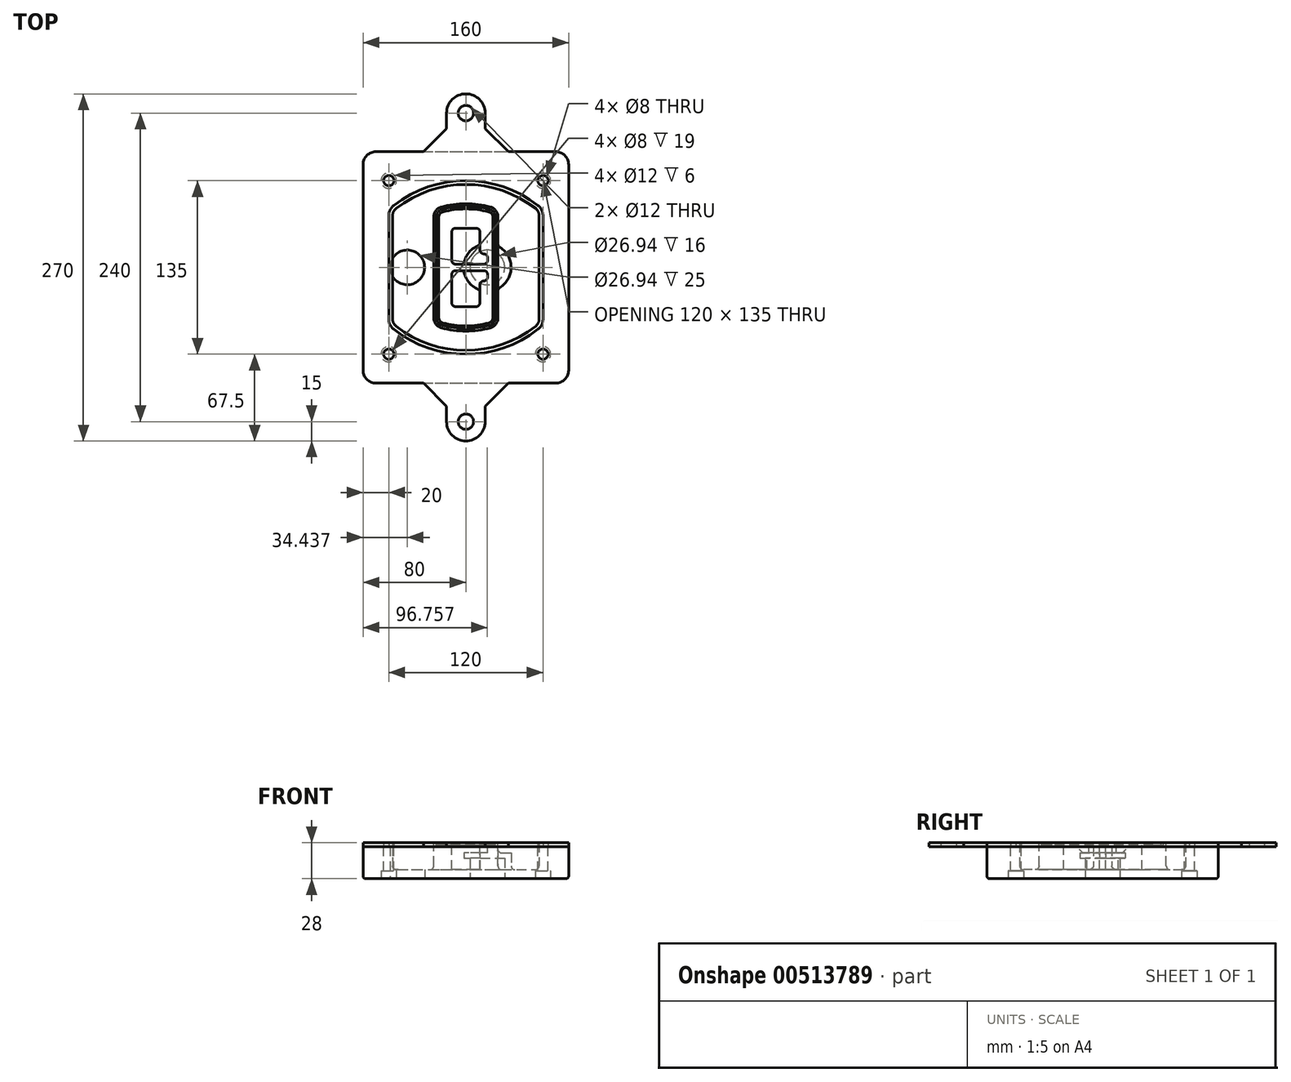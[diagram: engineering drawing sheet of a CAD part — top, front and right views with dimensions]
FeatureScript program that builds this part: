
annotation { "Feature Type Name" : "Feature", "Feature Type Description" : "" }
export const myFeature = defineFeature(function(context is Context, id is Id, definition is map)
    precondition{}
    {
        {
            var Q0;
            Q0=qCreatedBy(makeId("Top.planeOp"),FACE);
            var sketch = newSketch(context, id + "F0", { "sketchPlane" : qUnion([Q0])});
            skPoint(sketch, "E0.rect.middle", {"position": v(0, 0) * mm});
            skLineSegment(sketch, "E1.bottom", {"start": v(-70, -90) * mm, "end": v(70, -90) * mm});
            skLineSegment(sketch, "E1.top", {"start": v(-70, 90) * mm, "end": v(70, 90) * mm});
            skLineSegment(sketch, "E1.left", {"start": v(-80, -80) * mm, "end": v(-80, 80) * mm});
            skLineSegment(sketch, "E1.right", {"start": v(80, -80) * mm, "end": v(80, 80) * mm});
            skLineSegment(sketch, "E2", {"start": v(-80, 90) * mm, "end": v(80, -90) * mm, "construction": true});
            skLineSegment(sketch, "E3", {"start": v(80, 90) * mm, "end": v(-80, -90) * mm, "construction": true});
            skCircle(sketch, "E4", {"center": v(-60, 67.5) * mm, "radius": 4 * mm});
            skCircle(sketch, "E5", {"center": v(60, 67.5) * mm, "radius": 4 * mm});
            skCircle(sketch, "E6", {"center": v(60, -67.5) * mm, "radius": 4 * mm});
            skCircle(sketch, "E7", {"center": v(-60, -67.5) * mm, "radius": 4 * mm});
            skLineSegment(sketch, "E8", {"start": v(-60, 67.5) * mm, "end": v(60, 67.5) * mm, "construction": true});
            skLineSegment(sketch, "E9", {"start": v(60, 67.5) * mm, "end": v(60, -67.5) * mm, "construction": true});
            skLineSegment(sketch, "E10", {"start": v(60, -67.5) * mm, "end": v(-60, -67.5) * mm, "construction": true});
            skLineSegment(sketch, "E11", {"start": v(-60, -67.5) * mm, "end": v(-60, 67.5) * mm, "construction": true});
            skLineSegment(sketch, "E12", {"start": v(-60, 40.3) * mm, "end": v(-60, -40.3) * mm});
            skLineSegment(sketch, "E13", {"start": v(60, 40.3) * mm, "end": v(60, -40.3) * mm});
            skArc(sketch, "E14", {"start": v(56.15, 48.18) * mm, "mid": v(0, 67.5) * mm, "end": v(-56.15, 48.18) * mm});
            skArc(sketch, "E15", {"start": v(-56.15, -48.18) * mm, "mid": v(0, -67.5) * mm, "end": v(56.15, -48.18) * mm});
            skLineSegment(sketch, "E16", {"start": v(-60, 0) * mm, "end": v(60, 0) * mm, "construction": true});
            skPoint(sketch, "E17.visualSharp", {"position": v(-60, -45) * mm});
            skArc(sketch, "E17.filletArc", {"start": v(-60, -40.3) * mm, "mid": v(-58.99, -44.68) * mm, "end": v(-56.15, -48.18) * mm});
            skPoint(sketch, "E18.visualSharp", {"position": v(-60, 45) * mm});
            skArc(sketch, "E18.filletArc", {"start": v(-56.15, 48.18) * mm, "mid": v(-58.99, 44.68) * mm, "end": v(-60, 40.3) * mm});
            skPoint(sketch, "E19.visualSharp", {"position": v(60, 45) * mm});
            skArc(sketch, "E19.filletArc", {"start": v(60, 40.3) * mm, "mid": v(58.99, 44.68) * mm, "end": v(56.15, 48.18) * mm});
            skPoint(sketch, "E20.visualSharp", {"position": v(60, -45) * mm});
            skArc(sketch, "E20.filletArc", {"start": v(56.15, -48.18) * mm, "mid": v(58.99, -44.68) * mm, "end": v(60, -40.3) * mm});
            skPoint(sketch, "E21.visualSharp", {"position": v(-80, 90) * mm});
            skArc(sketch, "E21.filletArc", {"start": v(-70, 90) * mm, "mid": v(-77.07, 87.07) * mm, "end": v(-80, 80) * mm});
            skPoint(sketch, "E22.visualSharp", {"position": v(80, 90) * mm});
            skArc(sketch, "E22.filletArc", {"start": v(80, 80) * mm, "mid": v(77.07, 87.07) * mm, "end": v(70, 90) * mm});
            skPoint(sketch, "E23.visualSharp", {"position": v(80, -90) * mm});
            skArc(sketch, "E23.filletArc", {"start": v(70, -90) * mm, "mid": v(77.07, -87.07) * mm, "end": v(80, -80) * mm});
            skPoint(sketch, "E24.visualSharp", {"position": v(-80, -90) * mm});
            skArc(sketch, "E24.filletArc", {"start": v(-80, -80) * mm, "mid": v(-77.07, -87.07) * mm, "end": v(-70, -90) * mm});
            skArc(sketch, "E25.0", {"start": v(57, 40.3) * mm, "mid": v(56.3, 43.36) * mm, "end": v(54.3, 45.81) * mm});
            skLineSegment(sketch, "E25.1", {"start": v(57, 40.3) * mm, "end": v(57, -40.3) * mm});
            skArc(sketch, "E25.2", {"start": v(54.3, -45.81) * mm, "mid": v(56.3, -43.36) * mm, "end": v(57, -40.3) * mm});
            skArc(sketch, "E25.3", {"start": v(-54.3, -45.81) * mm, "mid": v(0, -64.5) * mm, "end": v(54.3, -45.81) * mm});
            skArc(sketch, "E25.4", {"start": v(-57, -40.3) * mm, "mid": v(-56.3, -43.36) * mm, "end": v(-54.3, -45.81) * mm});
            skArc(sketch, "E25.5", {"start": v(54.3, 45.81) * mm, "mid": v(0, 64.5) * mm, "end": v(-54.3, 45.81) * mm});
            skLineSegment(sketch, "E25.6", {"start": v(-57, 40.3) * mm, "end": v(-57, -40.3) * mm});
            skArc(sketch, "E25.7", {"start": v(-54.3, 45.81) * mm, "mid": v(-56.3, 43.36) * mm, "end": v(-57, 40.3) * mm});
            skArc(sketch, "E26.0", {"start": v(-58.62, 51.33) * mm, "mid": v(-62.58, 46.43) * mm, "end": v(-64, 40.3) * mm});
            skArc(sketch, "E26.1", {"start": v(58.62, 51.33) * mm, "mid": v(0, 71.5) * mm, "end": v(-58.62, 51.33) * mm});
            skArc(sketch, "E26.2", {"start": v(64, 40.3) * mm, "mid": v(62.58, 46.43) * mm, "end": v(58.62, 51.33) * mm});
            skLineSegment(sketch, "E26.3", {"start": v(64, 40.3) * mm, "end": v(64, -40.3) * mm});
            skArc(sketch, "E26.4", {"start": v(58.62, -51.33) * mm, "mid": v(62.58, -46.43) * mm, "end": v(64, -40.3) * mm});
            skLineSegment(sketch, "E26.5", {"start": v(-64, 40.3) * mm, "end": v(-64, -40.3) * mm});
            skArc(sketch, "E26.6", {"start": v(-58.62, -51.33) * mm, "mid": v(0, -71.5) * mm, "end": v(58.62, -51.33) * mm});
            skArc(sketch, "E26.7", {"start": v(-64, -40.3) * mm, "mid": v(-62.58, -46.43) * mm, "end": v(-58.62, -51.33) * mm});
            skSolve(sketch);
        }
        {
            var Q0;
            Q0=makeQuery(id+"F0.imprint","IMPRINT",FACE,{"disambiguationData":[TD([[makeQuery(id+"F0.imprint","IMPRINT",EDGE,{"derivedFrom":sQuery(id+"F0.wireOp",EDGE,"E1.bottom")}),1.0]])]});
            var Q1;
            Q1=makeQuery(id+"F0.imprint","IMPRINT",FACE,{"disambiguationData":[TD([[makeQuery(id+"F0.imprint","IMPRINT",EDGE,{"derivedFrom":sQuery(id+"F0.wireOp",EDGE,"E12")}),1.0]])]});
            var Q2;
            Q2=makeQuery(id+"F0.imprint","IMPRINT",FACE,{"disambiguationData":[TD([[makeQuery(id+"F0.imprint","IMPRINT",EDGE,{"derivedFrom":sQuery(id+"F0.wireOp",EDGE,"E25.0")}),1.0]])]});
            var Q3;
            Q3=makeQuery(id+"F0.imprint","IMPRINT",FACE,{"disambiguationData":[TD([[makeQuery(id+"F0.imprint","IMPRINT",EDGE,{"derivedFrom":sQuery(id+"F0.wireOp",EDGE,"E12")}),-1.0]])]});
            extrude(context, id + "F1", {"entities" : qUnion([Q0, Q1, Q2, Q3]), "oppositeDirection" : true, "depth" : 25 * mm});
        }
        {
            var Q0;
            Q0=makeQuery(id+"F0.imprint","IMPRINT",FACE,{"disambiguationData":[TD([[makeQuery(id+"F0.imprint","IMPRINT",EDGE,{"derivedFrom":sQuery(id+"F0.wireOp",EDGE,"E12")}),1.0]])]});
            extrude(context, id + "F2", {"entities" : qUnion([Q0]), "operationType" : NewBodyOperationType.ADD, "depth" : 3 * mm});
        }
        {
            var Q0;
            Q0=makeQuery(id+"F0.imprint","IMPRINT",FACE,{"disambiguationData":[TD([[makeQuery(id+"F0.imprint","IMPRINT",EDGE,{"derivedFrom":sQuery(id+"F0.wireOp",EDGE,"E25.0")}),1.0]])]});
            extrude(context, id + "F3", {"entities" : qUnion([Q0]), "operationType" : NewBodyOperationType.REMOVE, "oppositeDirection" : true, "depth" : 18 * mm});
        }
        {
            var Q0;
            Q0=makeQuery(id+"F2.opExtrude","CAP_FACE",FACE,{"disambiguationData":[OSD([sQuery(id+"F0.wireOp",EDGE,"E12"),sQuery(id+"F0.wireOp",EDGE,"E13"),sQuery(id+"F0.wireOp",EDGE,"E14"),sQuery(id+"F0.wireOp",EDGE,"E15"),sQuery(id+"F0.wireOp",EDGE,"E17.filletArc"),sQuery(id+"F0.wireOp",EDGE,"E18.filletArc"),sQuery(id+"F0.wireOp",EDGE,"E19.filletArc"),sQuery(id+"F0.wireOp",EDGE,"E20.filletArc"),sQuery(id+"F0.wireOp",EDGE,"E25.0"),sQuery(id+"F0.wireOp",EDGE,"E25.1"),sQuery(id+"F0.wireOp",EDGE,"E25.2"),sQuery(id+"F0.wireOp",EDGE,"E25.3"),sQuery(id+"F0.wireOp",EDGE,"E25.4"),sQuery(id+"F0.wireOp",EDGE,"E25.5"),sQuery(id+"F0.wireOp",EDGE,"E25.6"),sQuery(id+"F0.wireOp",EDGE,"E25.7")])],"isStart":false});
            var sketch = newSketch(context, id + "F4", { "sketchPlane" : qUnion([Q0])});
            skArc(sketch, "E27.0", {"start": v(-19.08, -46.97) * mm, "mid": v(0, -49.5) * mm, "end": v(19.08, -46.97) * mm});
            skArc(sketch, "E28.0", {"start": v(19.08, 46.97) * mm, "mid": v(0, 49.5) * mm, "end": v(-19.08, 46.97) * mm});
            skLineSegment(sketch, "E29", {"start": v(-25, 39.25) * mm, "end": v(-25, -39.25) * mm});
            skLineSegment(sketch, "E30", {"start": v(25, 39.25) * mm, "end": v(25, -39.25) * mm});
            skLineSegment(sketch, "E31", {"start": v(-25, 45.1) * mm, "end": v(25, 45.1) * mm, "construction": true});
            skLineSegment(sketch, "E32", {"start": v(-25, -45.1) * mm, "end": v(25, -45.1) * mm, "construction": true});
            skPoint(sketch, "E33.visualSharp", {"position": v(-25, 45.1) * mm});
            skArc(sketch, "E33.filletArc", {"start": v(-19.08, 46.97) * mm, "mid": v(-23.35, 44.11) * mm, "end": v(-25, 39.25) * mm});
            skPoint(sketch, "E34.visualSharp", {"position": v(25, 45.1) * mm});
            skArc(sketch, "E34.filletArc", {"start": v(25, 39.25) * mm, "mid": v(23.35, 44.11) * mm, "end": v(19.08, 46.97) * mm});
            skPoint(sketch, "E35.visualSharp", {"position": v(25, -45.1) * mm});
            skArc(sketch, "E35.filletArc", {"start": v(19.08, -46.97) * mm, "mid": v(23.35, -44.11) * mm, "end": v(25, -39.25) * mm});
            skPoint(sketch, "E36.visualSharp", {"position": v(-25, -45.1) * mm});
            skArc(sketch, "E36.filletArc", {"start": v(-25, -39.25) * mm, "mid": v(-23.35, -44.11) * mm, "end": v(-19.08, -46.97) * mm});
            skArc(sketch, "E37.0", {"start": v(54.3, 45.81) * mm, "mid": v(0, 64.5) * mm, "end": v(-54.3, 45.81) * mm});
            skArc(sketch, "E37.1", {"start": v(-54.3, 45.81) * mm, "mid": v(-56.3, 43.36) * mm, "end": v(-57, 40.3) * mm});
            skLineSegment(sketch, "E37.2", {"start": v(-57, 40.3) * mm, "end": v(-57, -40.3) * mm});
            skArc(sketch, "E37.3", {"start": v(-57, -40.3) * mm, "mid": v(-56.3, -43.36) * mm, "end": v(-54.3, -45.81) * mm});
            skArc(sketch, "E37.4", {"start": v(-54.3, -45.81) * mm, "mid": v(0, -64.5) * mm, "end": v(54.3, -45.81) * mm});
            skArc(sketch, "E37.5", {"start": v(54.3, -45.81) * mm, "mid": v(56.3, -43.36) * mm, "end": v(57, -40.3) * mm});
            skLineSegment(sketch, "E37.6", {"start": v(57, 40.3) * mm, "end": v(57, -40.3) * mm});
            skArc(sketch, "E37.7", {"start": v(57, 40.3) * mm, "mid": v(56.3, 43.36) * mm, "end": v(54.3, 45.81) * mm});
            skLineSegment(sketch, "E38.0", {"start": v(23, 39.25) * mm, "end": v(23, -39.25) * mm});
            skArc(sketch, "E38.1", {"start": v(18.56, -45.04) * mm, "mid": v(21.76, -42.9) * mm, "end": v(23, -39.25) * mm});
            skArc(sketch, "E38.2", {"start": v(-18.56, -45.04) * mm, "mid": v(0, -47.5) * mm, "end": v(18.56, -45.04) * mm});
            skArc(sketch, "E38.3", {"start": v(-23, -39.25) * mm, "mid": v(-21.76, -42.9) * mm, "end": v(-18.56, -45.04) * mm});
            skLineSegment(sketch, "E38.4", {"start": v(-23, 39.25) * mm, "end": v(-23, -39.25) * mm});
            skArc(sketch, "E38.5", {"start": v(23, 39.25) * mm, "mid": v(21.76, 42.9) * mm, "end": v(18.56, 45.04) * mm});
            skArc(sketch, "E38.6", {"start": v(-18.56, 45.04) * mm, "mid": v(-21.76, 42.9) * mm, "end": v(-23, 39.25) * mm});
            skArc(sketch, "E38.7", {"start": v(18.56, 45.04) * mm, "mid": v(0, 47.5) * mm, "end": v(-18.56, 45.04) * mm});
            skArc(sketch, "E39.0", {"start": v(21, 39.25) * mm, "mid": v(20.18, 41.68) * mm, "end": v(18.04, 43.1) * mm});
            skLineSegment(sketch, "E39.1", {"start": v(21, 39.25) * mm, "end": v(21, -39.25) * mm});
            skArc(sketch, "E39.2", {"start": v(18.04, -43.1) * mm, "mid": v(20.18, -41.68) * mm, "end": v(21, -39.25) * mm});
            skArc(sketch, "E39.3", {"start": v(-18.04, -43.1) * mm, "mid": v(0, -45.5) * mm, "end": v(18.04, -43.1) * mm});
            skArc(sketch, "E39.4", {"start": v(-21, -39.25) * mm, "mid": v(-20.18, -41.68) * mm, "end": v(-18.04, -43.1) * mm});
            skArc(sketch, "E39.5", {"start": v(18.04, 43.1) * mm, "mid": v(0, 45.5) * mm, "end": v(-18.04, 43.1) * mm});
            skLineSegment(sketch, "E39.6", {"start": v(-21, 39.25) * mm, "end": v(-21, -39.25) * mm});
            skArc(sketch, "E39.7", {"start": v(-18.04, 43.1) * mm, "mid": v(-20.18, 41.68) * mm, "end": v(-21, 39.25) * mm});
            skLineSegment(sketch, "E40", {"start": v(-25, 0) * mm, "end": v(25, 0) * mm, "construction": true});
            skLineSegment(sketch, "E41", {"start": v(-11, 5.5) * mm, "end": v(-11, 27.5) * mm});
            skLineSegment(sketch, "E42", {"start": v(-8, 30.5) * mm, "end": v(8, 30.5) * mm});
            skLineSegment(sketch, "E43", {"start": v(11, 27.5) * mm, "end": v(11, 13.5) * mm});
            skLineSegment(sketch, "E44", {"start": v(14, 10.5) * mm, "end": v(14, 10.5) * mm});
            skLineSegment(sketch, "E45", {"start": v(17, 7.5) * mm, "end": v(17, 5.5) * mm});
            skLineSegment(sketch, "E46", {"start": v(14, 2.5) * mm, "end": v(-8, 2.5) * mm});
            skPoint(sketch, "E47.visualSharp", {"position": v(-11, 30.5) * mm});
            skArc(sketch, "E47.filletArc", {"start": v(-8, 30.5) * mm, "mid": v(-10.12, 29.62) * mm, "end": v(-11, 27.5) * mm});
            skPoint(sketch, "E48.visualSharp", {"position": v(11, 30.5) * mm});
            skArc(sketch, "E48.filletArc", {"start": v(11, 27.5) * mm, "mid": v(10.12, 29.62) * mm, "end": v(8, 30.5) * mm});
            skPoint(sketch, "E49.visualSharp", {"position": v(11, 10.5) * mm});
            skArc(sketch, "E49.filletArc", {"start": v(11, 13.5) * mm, "mid": v(11.88, 11.38) * mm, "end": v(14, 10.5) * mm});
            skPoint(sketch, "E50.visualSharp", {"position": v(17, 10.5) * mm});
            skArc(sketch, "E50.filletArc", {"start": v(17, 7.5) * mm, "mid": v(16.12, 9.62) * mm, "end": v(14, 10.5) * mm});
            skPoint(sketch, "E51.visualSharp", {"position": v(17, 2.5) * mm});
            skArc(sketch, "E51.filletArc", {"start": v(14, 2.5) * mm, "mid": v(16.12, 3.38) * mm, "end": v(17, 5.5) * mm});
            skPoint(sketch, "E52.visualSharp", {"position": v(-11, 2.5) * mm});
            skArc(sketch, "E52.filletArc", {"start": v(-11, 5.5) * mm, "mid": v(-10.12, 3.38) * mm, "end": v(-8, 2.5) * mm});
            skLineSegment(sketch, "E53.0.MirrorCS", {"start": v(14, -2.5) * mm, "end": v(-8, -2.5) * mm});
            skArc(sketch, "E54.0.MirrorCS", {"start": v(-11, -5.5) * mm, "mid": v(-10.12, -3.38) * mm, "end": v(-8, -2.5) * mm});
            skLineSegment(sketch, "E55.0.MirrorCS", {"start": v(-11, -5.5) * mm, "end": v(-11, -27.5) * mm});
            skArc(sketch, "E56.0.MirrorCS", {"start": v(-8, -30.5) * mm, "mid": v(-10.12, -29.62) * mm, "end": v(-11, -27.5) * mm});
            skLineSegment(sketch, "E57.0.MirrorCS", {"start": v(-8, -30.5) * mm, "end": v(8, -30.5) * mm});
            skArc(sketch, "E58.0.MirrorCS", {"start": v(11, -27.5) * mm, "mid": v(10.12, -29.62) * mm, "end": v(8, -30.5) * mm});
            skLineSegment(sketch, "E59.0.MirrorCS", {"start": v(11, -27.5) * mm, "end": v(11, -13.5) * mm});
            skArc(sketch, "E60.0.MirrorCS", {"start": v(11, -13.5) * mm, "mid": v(11.88, -11.38) * mm, "end": v(14, -10.5) * mm});
            skArc(sketch, "E61.0.MirrorCS", {"start": v(17, -7.5) * mm, "mid": v(16.12, -9.62) * mm, "end": v(14, -10.5) * mm});
            skLineSegment(sketch, "E62.0.MirrorCS", {"start": v(17, -7.5) * mm, "end": v(17, -5.5) * mm});
            skArc(sketch, "E63.0.MirrorCS", {"start": v(14, -2.5) * mm, "mid": v(16.12, -3.38) * mm, "end": v(17, -5.5) * mm});
            skSolve(sketch);
        }
        {
            var Q0;
            Q0=makeQuery(id+"F4.imprint","IMPRINT",FACE,{"disambiguationData":[TD([[makeQuery(id+"F4.imprint","IMPRINT",EDGE,{"derivedFrom":sQuery(id+"F4.wireOp",EDGE,"E27.0")}),1.0]])]});
            var Q1;
            Q1=makeQuery(id+"F4.imprint","IMPRINT",FACE,{"disambiguationData":[TD([[makeQuery(id+"F4.imprint","IMPRINT",EDGE,{"derivedFrom":sQuery(id+"F4.wireOp",EDGE,"E38.0")}),-1.0]])]});
            var Q2;
            Q2=makeQuery(id+"F4.imprint","IMPRINT",FACE,{"disambiguationData":[TD([[makeQuery(id+"F4.imprint","IMPRINT",EDGE,{"derivedFrom":sQuery(id+"F4.wireOp",EDGE,"E39.0")}),1.0]])]});
            extrude(context, id + "F5", {"entities" : qUnion([Q0, Q1, Q2]), "operationType" : NewBodyOperationType.ADD, "endBound" : BoundingType.UP_TO_NEXT, "oppositeDirection" : true, "depth" : 25 * mm});
        }
        {
            var Q0;
            Q0=makeQuery(id+"F4.imprint","IMPRINT",FACE,{"disambiguationData":[TD([[makeQuery(id+"F4.imprint","IMPRINT",EDGE,{"derivedFrom":sQuery(id+"F4.wireOp",EDGE,"E38.0")}),-1.0]])]});
            extrude(context, id + "F6", {"entities" : qUnion([Q0]), "operationType" : NewBodyOperationType.REMOVE, "oppositeDirection" : true, "depth" : 2 * mm});
        }
        {
            var Q0;
            Q0=makeQuery(id+"F1.opExtrude","CAP_FACE",FACE,{"disambiguationData":[OSD([sQuery(id+"F0.wireOp",EDGE,"E1.bottom"),sQuery(id+"F0.wireOp",EDGE,"E1.top"),sQuery(id+"F0.wireOp",EDGE,"E1.left"),sQuery(id+"F0.wireOp",EDGE,"E1.right"),sQuery(id+"F0.wireOp",EDGE,"E4"),sQuery(id+"F0.wireOp",EDGE,"E5"),sQuery(id+"F0.wireOp",EDGE,"E6"),sQuery(id+"F0.wireOp",EDGE,"E7"),sQuery(id+"F0.wireOp",EDGE,"E21.filletArc"),sQuery(id+"F0.wireOp",EDGE,"E22.filletArc"),sQuery(id+"F0.wireOp",EDGE,"E23.filletArc"),sQuery(id+"F0.wireOp",EDGE,"E24.filletArc")])],"isStart":false});
            var sketch = newSketch(context, id + "F7", { "sketchPlane" : qUnion([Q0])});
            skCircle(sketch, "E64", {"center": v(16.76, 0) * mm, "radius": 13.47 * mm});
            skCircle(sketch, "E65", {"center": v(-45.56, 0) * mm, "radius": 13.47 * mm});
            skLineSegment(sketch, "E66", {"start": v(80, 0) * mm, "end": v(-80, 0) * mm});
            skCircle(sketch, "E67", {"center": v(16.76, 0) * mm, "radius": 18.47 * mm});
            skCircle(sketch, "E68", {"center": v(60, -67.5) * mm, "radius": 6 * mm});
            skCircle(sketch, "E69", {"center": v(-60, -67.5) * mm, "radius": 6 * mm});
            skCircle(sketch, "E70", {"center": v(-60, 67.5) * mm, "radius": 6 * mm});
            skCircle(sketch, "E71", {"center": v(60, 67.5) * mm, "radius": 6 * mm});
            skSolve(sketch);
        }
        {
            var Q0;
            {var subQ1=sQuery(id+"F7.wireOp",EDGE,"E66");var subQ4=sQuery(id+"F7.wireOp",EDGE,"E64");var subQ6=makeQuery(id+"F7.imprint","INTERSECT",VERTEX,{"disambiguationData":[OD(0.0)],"derivedFrom":[subQ4,subQ1]});Q0=makeQuery(id+"F7.imprint","IMPRINT",FACE,{"disambiguationData":[TD([[makeQuery(id+"F7.imprint","IMPRINT",EDGE,{"disambiguationData":[TD([[subQ6,-1.0]])],"derivedFrom":subQ4}),-1.0]])]});}
            var Q1;
            {var subQ0=sQuery(id+"F7.wireOp",EDGE,"E66");var subQ1=sQuery(id+"F7.wireOp",EDGE,"E64");var subQ3=makeQuery(id+"F7.imprint","INTERSECT",VERTEX,{"disambiguationData":[OD(0.0)],"derivedFrom":[subQ1,subQ0]});Q1=makeQuery(id+"F7.imprint","IMPRINT",FACE,{"disambiguationData":[TD([[makeQuery(id+"F7.imprint","IMPRINT",EDGE,{"disambiguationData":[TD([[subQ3,-1.0]])],"derivedFrom":subQ1}),1.0]])]});}
            var Q2;
            {var subQ0=sQuery(id+"F7.wireOp",EDGE,"E66");var subQ1=sQuery(id+"F7.wireOp",EDGE,"E64");var subQ3=makeQuery(id+"F7.imprint","INTERSECT",VERTEX,{"disambiguationData":[OD(0.0)],"derivedFrom":[subQ1,subQ0]});Q2=makeQuery(id+"F7.imprint","IMPRINT",FACE,{"disambiguationData":[TD([[makeQuery(id+"F7.imprint","IMPRINT",EDGE,{"disambiguationData":[TD([[subQ3,1.0]])],"derivedFrom":subQ1}),1.0]])]});}
            var Q3;
            {var subQ1=sQuery(id+"F7.wireOp",EDGE,"E66");var subQ4=sQuery(id+"F7.wireOp",EDGE,"E64");var subQ6=makeQuery(id+"F7.imprint","INTERSECT",VERTEX,{"disambiguationData":[OD(0.0)],"derivedFrom":[subQ4,subQ1]});Q3=makeQuery(id+"F7.imprint","IMPRINT",FACE,{"disambiguationData":[TD([[makeQuery(id+"F7.imprint","IMPRINT",EDGE,{"disambiguationData":[TD([[subQ6,1.0]])],"derivedFrom":subQ4}),-1.0]])]});}
            extrude(context, id + "F8", {"entities" : qUnion([Q0, Q1, Q2, Q3]), "operationType" : NewBodyOperationType.ADD, "oppositeDirection" : true, "depth" : 20 * mm});
        }
        {
            var Q0;
            {var subQ0=sQuery(id+"F7.wireOp",EDGE,"E66");var subQ1=sQuery(id+"F7.wireOp",EDGE,"E64");var subQ3=makeQuery(id+"F7.imprint","INTERSECT",VERTEX,{"disambiguationData":[OD(0.0)],"derivedFrom":[subQ1,subQ0]});Q0=makeQuery(id+"F7.imprint","IMPRINT",FACE,{"disambiguationData":[TD([[makeQuery(id+"F7.imprint","IMPRINT",EDGE,{"disambiguationData":[TD([[subQ3,-1.0]])],"derivedFrom":subQ1}),1.0]])]});}
            var Q1;
            {var subQ0=sQuery(id+"F7.wireOp",EDGE,"E66");var subQ1=sQuery(id+"F7.wireOp",EDGE,"E64");var subQ3=makeQuery(id+"F7.imprint","INTERSECT",VERTEX,{"disambiguationData":[OD(0.0)],"derivedFrom":[subQ1,subQ0]});Q1=makeQuery(id+"F7.imprint","IMPRINT",FACE,{"disambiguationData":[TD([[makeQuery(id+"F7.imprint","IMPRINT",EDGE,{"disambiguationData":[TD([[subQ3,1.0]])],"derivedFrom":subQ1}),1.0]])]});}
            extrude(context, id + "F9", {"entities" : qUnion([Q0, Q1]), "operationType" : NewBodyOperationType.REMOVE, "oppositeDirection" : true, "depth" : 16 * mm});
        }
        {
            var Q0;
            {var subQ0=sQuery(id+"F7.wireOp",EDGE,"E66");var subQ1=sQuery(id+"F7.wireOp",EDGE,"E65");var subQ3=makeQuery(id+"F7.imprint","INTERSECT",VERTEX,{"disambiguationData":[OD(0.0)],"derivedFrom":[subQ1,subQ0]});Q0=makeQuery(id+"F7.imprint","IMPRINT",FACE,{"disambiguationData":[TD([[makeQuery(id+"F7.imprint","IMPRINT",EDGE,{"disambiguationData":[TD([[subQ3,-1.0]])],"derivedFrom":subQ1}),1.0]])]});}
            var Q1;
            {var subQ0=sQuery(id+"F7.wireOp",EDGE,"E66");var subQ1=sQuery(id+"F7.wireOp",EDGE,"E65");var subQ3=makeQuery(id+"F7.imprint","INTERSECT",VERTEX,{"disambiguationData":[OD(0.0)],"derivedFrom":[subQ1,subQ0]});Q1=makeQuery(id+"F7.imprint","IMPRINT",FACE,{"disambiguationData":[TD([[makeQuery(id+"F7.imprint","IMPRINT",EDGE,{"disambiguationData":[TD([[subQ3,1.0]])],"derivedFrom":subQ1}),1.0]])]});}
            extrude(context, id + "F10", {"entities" : qUnion([Q0, Q1]), "operationType" : NewBodyOperationType.REMOVE, "oppositeDirection" : true, "depth" : 25 * mm});
        }
        {
            var Q0;
            Q0=makeQuery(id+"F7.imprint","IMPRINT",FACE,{"disambiguationData":[TD([[makeQuery(id+"F7.imprint","IMPRINT",EDGE,{"derivedFrom":sQuery(id+"F7.wireOp",EDGE,"E68")}),1.0]])]});
            var Q1;
            Q1=makeQuery(id+"F7.imprint","IMPRINT",FACE,{"disambiguationData":[TD([[makeQuery(id+"F7.imprint","IMPRINT",EDGE,{"derivedFrom":makeQuery(id+"F1.opExtrude","CAP_EDGE",EDGE,{"disambiguationData":[OSD([sQuery(id+"F0.wireOp",EDGE,"E5")])],"isStart":false})}),-1.0]])]});
            var Q2;
            Q2=makeQuery(id+"F7.imprint","IMPRINT",FACE,{"disambiguationData":[TD([[makeQuery(id+"F7.imprint","IMPRINT",EDGE,{"derivedFrom":sQuery(id+"F7.wireOp",EDGE,"E69")}),1.0]])]});
            var Q3;
            Q3=makeQuery(id+"F7.imprint","IMPRINT",FACE,{"disambiguationData":[TD([[makeQuery(id+"F7.imprint","IMPRINT",EDGE,{"derivedFrom":makeQuery(id+"F1.opExtrude","CAP_EDGE",EDGE,{"disambiguationData":[OSD([sQuery(id+"F0.wireOp",EDGE,"E4")])],"isStart":false})}),-1.0]])]});
            var Q4;
            Q4=makeQuery(id+"F7.imprint","IMPRINT",FACE,{"disambiguationData":[TD([[makeQuery(id+"F7.imprint","IMPRINT",EDGE,{"derivedFrom":sQuery(id+"F7.wireOp",EDGE,"E70")}),1.0]])]});
            var Q5;
            Q5=makeQuery(id+"F7.imprint","IMPRINT",FACE,{"disambiguationData":[TD([[makeQuery(id+"F7.imprint","IMPRINT",EDGE,{"derivedFrom":makeQuery(id+"F1.opExtrude","CAP_EDGE",EDGE,{"disambiguationData":[OSD([sQuery(id+"F0.wireOp",EDGE,"E7")])],"isStart":false})}),-1.0]])]});
            var Q6;
            Q6=makeQuery(id+"F7.imprint","IMPRINT",FACE,{"disambiguationData":[TD([[makeQuery(id+"F7.imprint","IMPRINT",EDGE,{"derivedFrom":sQuery(id+"F7.wireOp",EDGE,"E71")}),1.0]])]});
            var Q7;
            Q7=makeQuery(id+"F7.imprint","IMPRINT",FACE,{"disambiguationData":[TD([[makeQuery(id+"F7.imprint","IMPRINT",EDGE,{"derivedFrom":makeQuery(id+"F1.opExtrude","CAP_EDGE",EDGE,{"disambiguationData":[OSD([sQuery(id+"F0.wireOp",EDGE,"E6")])],"isStart":false})}),-1.0]])]});
            extrude(context, id + "F11", {"entities" : qUnion([Q0, Q1, Q2, Q3, Q4, Q5, Q6, Q7]), "operationType" : NewBodyOperationType.REMOVE, "oppositeDirection" : true, "depth" : 6 * mm});
        }
        {
            var Q0;
            Q0=makeQuery(id+"F9.boolean.opBoolean","COPY",FACE,{"derivedFrom":makeQuery(id+"F9.opExtrude","CAP_FACE",FACE,{"disambiguationData":[OSD([sQuery(id+"F7.wireOp",EDGE,"E64")])],"isStart":false})});
            var sketch = newSketch(context, id + "F12", { "sketchPlane" : qUnion([Q0])});
            skArc(sketch, "E72.0", {"start": v(11, 17.55) * mm, "mid": v(2.57, 11.82) * mm, "end": v(-1.54, 2.5) * mm});
            skArc(sketch, "E72.1", {"start": v(-1.54, -2.5) * mm, "mid": v(2.57, -11.82) * mm, "end": v(11, -17.55) * mm});
            skLineSegment(sketch, "E73", {"start": v(-1.54, -2.5) * mm, "end": v(14, -2.5) * mm});
            skLineSegment(sketch, "E74.0", {"start": v(14, 2.5) * mm, "end": v(-1.54, 2.5) * mm});
            skArc(sketch, "E74.1", {"start": v(14, 2.5) * mm, "mid": v(16.12, 3.38) * mm, "end": v(17, 5.5) * mm});
            skLineSegment(sketch, "E74.2", {"start": v(17, 7.5) * mm, "end": v(17, 5.5) * mm});
            skArc(sketch, "E74.3", {"start": v(17, 7.5) * mm, "mid": v(16.12, 9.62) * mm, "end": v(14, 10.5) * mm});
            skArc(sketch, "E74.4", {"start": v(11, 13.5) * mm, "mid": v(11.88, 11.38) * mm, "end": v(14, 10.5) * mm});
            skLineSegment(sketch, "E74.5", {"start": v(11, 17.55) * mm, "end": v(11, 13.5) * mm});
            skLineSegment(sketch, "E74.7", {"start": v(14, -2.5) * mm, "end": v(-1.54, -2.5) * mm});
            skArc(sketch, "E74.8", {"start": v(14, -2.5) * mm, "mid": v(16.12, -3.38) * mm, "end": v(17, -5.5) * mm});
            skLineSegment(sketch, "E74.9", {"start": v(17, -7.5) * mm, "end": v(17, -5.5) * mm});
            skArc(sketch, "E74.10", {"start": v(17, -7.5) * mm, "mid": v(16.12, -9.62) * mm, "end": v(14, -10.5) * mm});
            skArc(sketch, "E74.11", {"start": v(11, -13.5) * mm, "mid": v(11.88, -11.38) * mm, "end": v(14, -10.5) * mm});
            skLineSegment(sketch, "E74.12", {"start": v(11, -17.55) * mm, "end": v(11, -13.5) * mm});
            skPoint(sketch, "E75.orphan", {"position": v(11, -27.5) * mm});
            skPoint(sketch, "E76.orphan", {"position": v(-8, -2.5) * mm});
            skPoint(sketch, "E77.orphan", {"position": v(-8, 2.5) * mm});
            skPoint(sketch, "E78.orphan", {"position": v(11, 27.5) * mm});
            skSolve(sketch);
        }
        {
            var Q0;
            {var subQ7=sQuery(id+"F12.wireOp",EDGE,"E72.0");var subQ14=sQuery(id+"F12.wireOp",EDGE,"E72.1");var subQ16=sQuery(id+"F12.wireOp",EDGE,"E74.1");var subQ18=sQuery(id+"F12.wireOp",EDGE,"E74.8");Q0=qUnion([makeQuery(id+"F12.imprint","IMPRINT",FACE,{"disambiguationData":[TD([[makeQuery(id+"F12.imprint","IMPRINT",EDGE,{"derivedFrom":subQ7}),1.0]])]}),makeQuery(id+"F12.imprint","IMPRINT",FACE,{"disambiguationData":[TD([[makeQuery(id+"F12.imprint","IMPRINT",EDGE,{"derivedFrom":subQ14}),1.0]])]}),makeQuery(id+"F12.imprint","IMPRINT",FACE,{"disambiguationData":[TD([[makeQuery(id+"F12.imprint","IMPRINT",EDGE,{"derivedFrom":subQ16}),1.0]])]}),makeQuery(id+"F12.imprint","IMPRINT",FACE,{"disambiguationData":[TD([[makeQuery(id+"F12.imprint","IMPRINT",EDGE,{"derivedFrom":subQ18}),-1.0]])]})]);}
            var Q1;
            Q1=makeQuery(id+"F5.boolean.opBoolean","SPLIT",FACE,{"disambiguationData":[TD([makeQuery(id+"F5.opExtrude","SWEPT_FACE",FACE,{"disambiguationData":[OSD([sQuery(id+"F4.wireOp",EDGE,"E41")])]})])],"derivedFrom":makeQuery(id+"F3.boolean.opBoolean","COPY",FACE,{"derivedFrom":makeQuery(id+"F3.opExtrude","CAP_FACE",FACE,{"disambiguationData":[OSD([sQuery(id+"F0.wireOp",EDGE,"E25.0"),sQuery(id+"F0.wireOp",EDGE,"E25.1"),sQuery(id+"F0.wireOp",EDGE,"E25.2"),sQuery(id+"F0.wireOp",EDGE,"E25.3"),sQuery(id+"F0.wireOp",EDGE,"E25.4"),sQuery(id+"F0.wireOp",EDGE,"E25.5"),sQuery(id+"F0.wireOp",EDGE,"E25.6"),sQuery(id+"F0.wireOp",EDGE,"E25.7")])],"isStart":false})})});
            extrude(context, id + "F13", {"entities" : qUnion([Q0]), "operationType" : NewBodyOperationType.REMOVE, "endBound" : BoundingType.UP_TO_SURFACE, "endBoundEntityFace" : qUnion([Q1]), "depth" : 25 * mm});
        }
        {
            var Q0;
            Q0=makeQuery(id+"F3.boolean.opBoolean","COPY",EDGE,{"derivedFrom":makeQuery(id+"F3.opExtrude","CAP_EDGE",EDGE,{"disambiguationData":[OSD([sQuery(id+"F0.wireOp",EDGE,"E25.6")])],"isStart":false})});
            var Q1;
            Q1=makeQuery(id+"F8.boolean.opBoolean","INTERSECT",EDGE,{"derivedFrom":[makeQuery(id+"F5.opExtrude","SWEPT_FACE",FACE,{"disambiguationData":[OSD([sQuery(id+"F4.wireOp",EDGE,"E30")])]}),makeQuery(id+"F8.opExtrude","CAP_FACE",FACE,{"disambiguationData":[OSD([sQuery(id+"F7.wireOp",EDGE,"E67")])],"isStart":false})]});
            var Q2;
            Q2=makeQuery(id+"F8.boolean.opBoolean","INTERSECT",EDGE,{"disambiguationData":[OD(1.0)],"derivedFrom":[makeQuery(id+"F5.opExtrude","SWEPT_FACE",FACE,{"disambiguationData":[OSD([sQuery(id+"F4.wireOp",EDGE,"E30")])]}),makeQuery(id+"F8.opExtrude","SWEPT_FACE",FACE,{"disambiguationData":[OSD([sQuery(id+"F7.wireOp",EDGE,"E67")])]})]});
            var Q3;
            {var subQ0=sQuery(id+"F4.wireOp",EDGE,"E30");Q3=makeQuery(id+"F8.boolean.opBoolean","SPLIT",EDGE,{"disambiguationData":[TD([makeQuery(id+"F5.opExtrude","SWEPT_FACE",FACE,{"disambiguationData":[OSD([sQuery(id+"F4.wireOp",EDGE,"E35.filletArc")])]})])],"derivedFrom":makeQuery(id+"F5.opExtrude","CAP_EDGE",EDGE,{"disambiguationData":[OSD([subQ0])],"isStart":false})});}
            var Q4;
            {var subQ0=sQuery(id+"F0.wireOp",EDGE,"E25.7");var subQ1=sQuery(id+"F0.wireOp",EDGE,"E25.1");var subQ2=sQuery(id+"F0.wireOp",EDGE,"E25.6");var subQ3=sQuery(id+"F0.wireOp",EDGE,"E25.5");var subQ4=sQuery(id+"F0.wireOp",EDGE,"E25.4");var subQ5=sQuery(id+"F0.wireOp",EDGE,"E25.0");var subQ6=sQuery(id+"F0.wireOp",EDGE,"E25.2");var subQ7=sQuery(id+"F0.wireOp",EDGE,"E25.3");Q4=makeQuery(id+"F8.boolean.opBoolean","INTERSECT",EDGE,{"derivedFrom":[makeQuery(id+"F5.boolean.opBoolean","SPLIT",FACE,{"disambiguationData":[TD([makeQuery(id+"F2.opExtrude","SWEPT_FACE",FACE,{"disambiguationData":[OSD([subQ5])]})])],"derivedFrom":makeQuery(id+"F3.boolean.opBoolean","COPY",FACE,{"derivedFrom":makeQuery(id+"F3.opExtrude","CAP_FACE",FACE,{"disambiguationData":[OSD([subQ5,subQ1,subQ6,subQ7,subQ4,subQ3,subQ2,subQ0])],"isStart":false})})}),makeQuery(id+"F8.opExtrude","SWEPT_FACE",FACE,{"disambiguationData":[OSD([sQuery(id+"F7.wireOp",EDGE,"E67")])]})]});}
            var Q5;
            Q5=makeQuery(id+"F8.boolean.opBoolean","INTERSECT",EDGE,{"disambiguationData":[OD(0.0)],"derivedFrom":[makeQuery(id+"F5.opExtrude","SWEPT_FACE",FACE,{"disambiguationData":[OSD([sQuery(id+"F4.wireOp",EDGE,"E30")])]}),makeQuery(id+"F8.opExtrude","SWEPT_FACE",FACE,{"disambiguationData":[OSD([sQuery(id+"F7.wireOp",EDGE,"E67")])]})]});
            fillet(context, id + "F14", {"entities" : qUnion([Q0, Q1, Q2, Q3, Q4, Q5]), "radius" : 3 * mm, "tangentPropagation" : true, "allowEdgeOverflow" : false});
        }
        {
            var Q0;
            Q0=makeQuery(id+"F1.opExtrude","CAP_EDGE",EDGE,{"disambiguationData":[OSD([sQuery(id+"F0.wireOp",EDGE,"E1.bottom")])],"isStart":false});
            fillet(context, id + "F15", {"entities" : qUnion([Q0]), "radius" : 2 * mm, "tangentPropagation" : true, "allowEdgeOverflow" : false});
        }
        {
            var Q0;
            {var subQ0=sQuery(id+"F0.wireOp",EDGE,"E21.filletArc");var subQ1=sQuery(id+"F0.wireOp",EDGE,"E7");var subQ2=sQuery(id+"F0.wireOp",EDGE,"E6");var subQ3=sQuery(id+"F0.wireOp",EDGE,"E5");var subQ4=sQuery(id+"F0.wireOp",EDGE,"E4");var subQ5=sQuery(id+"F0.wireOp",EDGE,"E22.filletArc");var subQ6=sQuery(id+"F0.wireOp",EDGE,"E1.bottom");var subQ7=sQuery(id+"F0.wireOp",EDGE,"E1.right");var subQ8=sQuery(id+"F0.wireOp",EDGE,"E1.top");var subQ9=sQuery(id+"F0.wireOp",EDGE,"E1.left");var subQ10=sQuery(id+"F0.wireOp",EDGE,"E23.filletArc");var subQ11=sQuery(id+"F0.wireOp",EDGE,"E24.filletArc");Q0=makeQuery(id+"F2.boolean.opBoolean","SPLIT",FACE,{"disambiguationData":[TD([makeQuery(id+"F1.opExtrude","SWEPT_FACE",FACE,{"disambiguationData":[OSD([subQ6])]})])],"derivedFrom":makeQuery(id+"F1.opExtrude","CAP_FACE",FACE,{"disambiguationData":[OSD([subQ6,subQ8,subQ9,subQ7,subQ4,subQ3,subQ2,subQ1,subQ0,subQ5,subQ10,subQ11])],"isStart":true})});}
            var sketch = newSketch(context, id + "F16", { "sketchPlane" : qUnion([Q0])});
            skLineSegment(sketch, "E79.0", {"start": v(-70, 90) * mm, "end": v(70, 90) * mm});
            skLineSegment(sketch, "E79.1", {"start": v(-80, -80) * mm, "end": v(-80, 80) * mm});
            skLineSegment(sketch, "E79.2", {"start": v(-70, -90) * mm, "end": v(70, -90) * mm});
            skLineSegment(sketch, "E79.3", {"start": v(80, -80) * mm, "end": v(80, 80) * mm});
            skLineSegment(sketch, "E79.4", {"start": v(60, 40.3) * mm, "end": v(60, -40.3) * mm});
            skArc(sketch, "E79.5", {"start": v(60, 40.3) * mm, "mid": v(58.99, 44.68) * mm, "end": v(56.15, 48.18) * mm});
            skArc(sketch, "E79.6", {"start": v(56.15, 48.18) * mm, "mid": v(0, 67.5) * mm, "end": v(-56.15, 48.18) * mm});
            skLineSegment(sketch, "E79.7", {"start": v(-60, 40.3) * mm, "end": v(-60, -40.3) * mm});
            skArc(sketch, "E79.8", {"start": v(-56.15, -48.18) * mm, "mid": v(0, -67.5) * mm, "end": v(56.15, -48.18) * mm});
            skArc(sketch, "E79.9", {"start": v(56.15, -48.18) * mm, "mid": v(58.99, -44.68) * mm, "end": v(60, -40.3) * mm});
            skArc(sketch, "E79.10", {"start": v(-56.15, 48.18) * mm, "mid": v(-58.99, 44.68) * mm, "end": v(-60, 40.3) * mm});
            skArc(sketch, "E79.11", {"start": v(-60, -40.3) * mm, "mid": v(-58.99, -44.68) * mm, "end": v(-56.15, -48.18) * mm});
            skCircle(sketch, "E79.12", {"center": v(-60, 67.5) * mm, "radius": 4 * mm});
            skCircle(sketch, "E79.13", {"center": v(60, 67.5) * mm, "radius": 4 * mm});
            skCircle(sketch, "E79.14", {"center": v(60, -67.5) * mm, "radius": 4 * mm});
            skCircle(sketch, "E79.15", {"center": v(-60, -67.5) * mm, "radius": 4 * mm});
            skArc(sketch, "E79.16", {"start": v(-80, -80) * mm, "mid": v(-77.07, -87.07) * mm, "end": v(-70, -90) * mm});
            skArc(sketch, "E79.17", {"start": v(-70, 90) * mm, "mid": v(-77.07, 87.07) * mm, "end": v(-80, 80) * mm});
            skArc(sketch, "E79.18", {"start": v(80, 80) * mm, "mid": v(77.07, 87.07) * mm, "end": v(70, 90) * mm});
            skArc(sketch, "E79.19", {"start": v(70, -90) * mm, "mid": v(77.07, -87.07) * mm, "end": v(80, -80) * mm});
            skLineSegment(sketch, "E80", {"start": v(0, 90) * mm, "end": v(0, 120) * mm, "construction": true});
            skPoint(sketch, "E80.endSnap0", {"position": v(0, 90) * mm});
            skCircle(sketch, "E81", {"center": v(0, 120) * mm, "radius": 6 * mm});
            skLineSegment(sketch, "E82", {"start": v(0, 90) * mm, "end": v(-28, 90) * mm});
            skLineSegment(sketch, "E83", {"start": v(0, 90) * mm, "end": v(33, 90) * mm});
            skLineSegment(sketch, "E84", {"start": v(0, -90) * mm, "end": v(0, -107.47) * mm});
            skLineSegment(sketch, "E85", {"start": v(-33, 90) * mm, "end": v(-15, 108) * mm});
            skLineSegment(sketch, "E86", {"start": v(-15, 108) * mm, "end": v(-15, 120) * mm});
            skArc(sketch, "E87", {"start": v(-15, 120) * mm, "mid": v(0, 135) * mm, "end": v(15, 120) * mm});
            skLineSegment(sketch, "E88", {"start": v(15, 120) * mm, "end": v(15, 108) * mm});
            skLineSegment(sketch, "E89", {"start": v(15, 108) * mm, "end": v(33, 90) * mm});
            skLineSegment(sketch, "E90", {"start": v(-111.23, 0) * mm, "end": v(110.85, 0) * mm, "construction": true});
            skPoint(sketch, "E90.endSnap0", {"position": v(60, 0) * mm});
            skLineSegment(sketch, "E91.MirrorCS", {"start": v(-33, -90) * mm, "end": v(-15, -108) * mm});
            skArc(sketch, "E92.MirrorCS", {"start": v(-15, -120) * mm, "mid": v(0, -135) * mm, "end": v(15, -120) * mm});
            skLineSegment(sketch, "E93.MirrorCS", {"start": v(-15, -108) * mm, "end": v(-15, -120) * mm});
            skLineSegment(sketch, "E94.MirrorCS", {"start": v(15, -120) * mm, "end": v(15, -108) * mm});
            skCircle(sketch, "E95.MirrorC", {"center": v(0, -120) * mm, "radius": 6 * mm});
            skLineSegment(sketch, "E96.MirrorCS", {"start": v(0, -90) * mm, "end": v(0, -120) * mm, "construction": true});
            skLineSegment(sketch, "E97.MirrorCS", {"start": v(15, -108) * mm, "end": v(33, -90) * mm});
            skSolve(sketch);
        }
        {
            var Q0;
            Q0 = qSketchRegion(id + "F16", true);
            var Q1;
            Q1=makeQuery(id+"F2.opExtrude","CAP_FACE",FACE,{"disambiguationData":[OSD([sQuery(id+"F0.wireOp",EDGE,"E12"),sQuery(id+"F0.wireOp",EDGE,"E13"),sQuery(id+"F0.wireOp",EDGE,"E14"),sQuery(id+"F0.wireOp",EDGE,"E15"),sQuery(id+"F0.wireOp",EDGE,"E17.filletArc"),sQuery(id+"F0.wireOp",EDGE,"E18.filletArc"),sQuery(id+"F0.wireOp",EDGE,"E19.filletArc"),sQuery(id+"F0.wireOp",EDGE,"E20.filletArc"),sQuery(id+"F0.wireOp",EDGE,"E25.0"),sQuery(id+"F0.wireOp",EDGE,"E25.1"),sQuery(id+"F0.wireOp",EDGE,"E25.2"),sQuery(id+"F0.wireOp",EDGE,"E25.3"),sQuery(id+"F0.wireOp",EDGE,"E25.4"),sQuery(id+"F0.wireOp",EDGE,"E25.5"),sQuery(id+"F0.wireOp",EDGE,"E25.6"),sQuery(id+"F0.wireOp",EDGE,"E25.7")])],"isStart":false});
            extrude(context, id + "F17", {"entities" : qUnion([Q0]), "endBound" : BoundingType.UP_TO_SURFACE, "depth" : 25 * mm, "endBoundEntityFace" : qUnion([Q1]), "offsetDistance" : 25 * mm});
        }
    });
